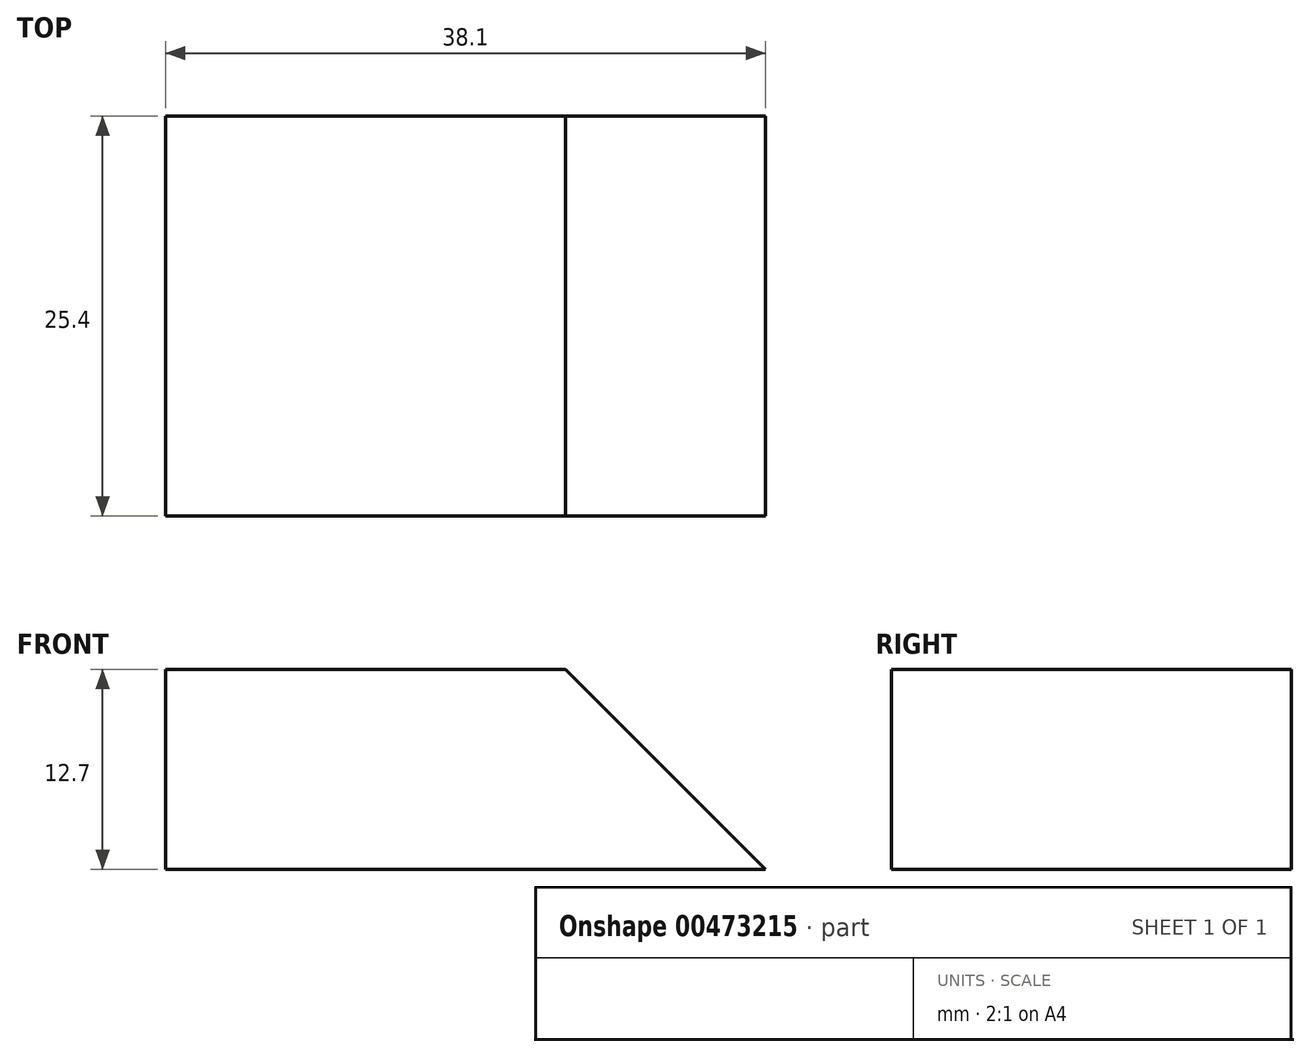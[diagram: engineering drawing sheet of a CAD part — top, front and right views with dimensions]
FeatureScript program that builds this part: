
annotation { "Feature Type Name" : "Feature", "Feature Type Description" : "" }
export const myFeature = defineFeature(function(context is Context, id is Id, definition is map)
    precondition{}
    {
        {
            var Q0;
            Q0=qCreatedBy(makeId("Front.planeOp"),FACE);
            var sketch = newSketch(context, id + "F0", { "sketchPlane" : qUnion([Q0])});
            skLineSegment(sketch, "E0", {"start": v(-30.54, 14.69) * mm, "end": v(-30.54, 1.99) * mm});
            skLineSegment(sketch, "E1", {"start": v(-30.54, 1.99) * mm, "end": v(7.56, 1.99) * mm});
            skLineSegment(sketch, "E2", {"start": v(7.56, 1.99) * mm, "end": v(-5.14, 14.69) * mm});
            skLineSegment(sketch, "E3", {"start": v(-5.14, 14.69) * mm, "end": v(-30.54, 14.69) * mm});
            skSolve(sketch);
        }
        {
            var Q0;
            Q0 = qSketchRegion(id + "F0", true);
            extrude(context, id + "F1", {"entities" : qUnion([Q0]), "depth" : 25.4 * mm});
        }
    });
